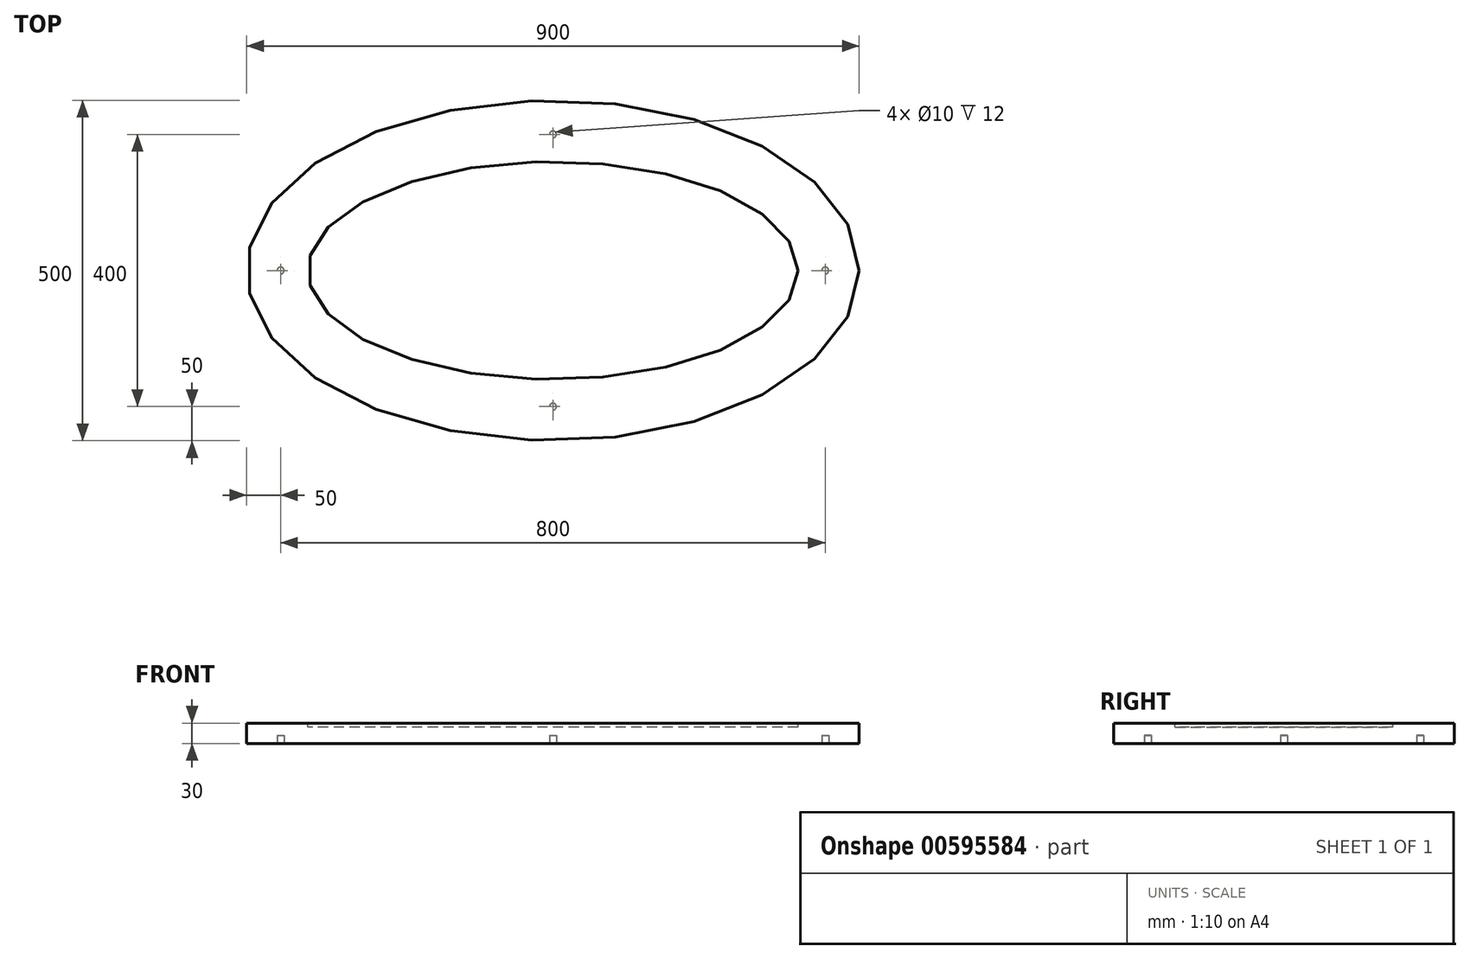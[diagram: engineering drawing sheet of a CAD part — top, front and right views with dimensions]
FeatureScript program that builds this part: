
annotation { "Feature Type Name" : "Feature", "Feature Type Description" : "" }
export const myFeature = defineFeature(function(context is Context, id is Id, definition is map)
    precondition{}
    {
        {
            var Q0;
            Q0=qCreatedBy(makeId("Top.planeOp"),FACE);
            var sketch = newSketch(context, id + "F0", { "sketchPlane" : qUnion([Q0])});
            skEllipse(sketch, "E0", {"center": v(0, 0) * mm, "majorRadius": 450 * mm, "minorRadius": 250 * mm, "majorAxis": v(1, 0)});
            skFitSpline(sketch, "E1.0", {"points": [v(349.97, -1.74) * mm, v(350.01, 0) * mm, v(349.97, 1.74) * mm, v(349.82, 4.08) * mm, v(349.42, 7.07) * mm, v(348.57, 10.9) * mm, v(347.27, 15.08) * mm, v(345.43, 19.64) * mm, v(342.94, 24.63) * mm, v(339.74, 30.04) * mm, v(335.72, 35.84) * mm, v(330.84, 41.98) * mm, v(325.03, 48.4) * mm, v(318.28, 55.05) * mm, v(310.55, 61.86) * mm, v(301.83, 68.75) * mm, v(293.75, 74.52) * mm, v(286.8, 79.12) * mm, v(281.33, 82.56) * mm, v(275.62, 85.98) * mm, v(269.67, 89.37) * mm, v(263.5, 92.72) * mm, v(257.12, 96) * mm, v(250.55, 99.23) * mm, v(241.54, 103.43) * mm, v(229.8, 108.51) * mm, v(215.03, 114.28) * mm, v(199.6, 119.7) * mm, v(178.22, 126.42) * mm, v(150.1, 133.81) * mm, v(120.4, 139.72) * mm, v(95.91, 143.5) * mm, v(77.2, 145.85) * mm, v(58.22, 147.69) * mm, v(42.2, 148.8) * mm, v(29.3, 149.42) * mm, v(19.56, 149.75) * mm, v(11.43, 149.92) * mm, v(4.9, 149.99) * mm, v(0, 150) * mm, v(-4.9, 149.99) * mm, v(-11.43, 149.92) * mm, v(-19.56, 149.75) * mm, v(-29.3, 149.42) * mm, v(-42.2, 148.8) * mm, v(-58.22, 147.69) * mm, v(-77.2, 145.85) * mm, v(-95.91, 143.5) * mm, v(-120.4, 139.72) * mm, v(-150.1, 133.81) * mm, v(-178.22, 126.42) * mm, v(-199.6, 119.7) * mm, v(-215.03, 114.28) * mm, v(-229.8, 108.51) * mm, v(-241.54, 103.43) * mm, v(-250.55, 99.23) * mm, v(-257.12, 96) * mm, v(-263.5, 92.72) * mm, v(-269.67, 89.37) * mm, v(-275.62, 85.98) * mm, v(-281.33, 82.56) * mm, v(-286.8, 79.12) * mm, v(-293.75, 74.52) * mm, v(-301.83, 68.75) * mm, v(-310.55, 61.86) * mm, v(-318.28, 55.05) * mm, v(-325.03, 48.4) * mm, v(-330.84, 41.98) * mm, v(-335.72, 35.84) * mm, v(-339.74, 30.04) * mm, v(-342.94, 24.63) * mm, v(-345.43, 19.64) * mm, v(-347.27, 15.08) * mm, v(-348.57, 10.9) * mm, v(-349.42, 7.07) * mm, v(-349.82, 4.08) * mm, v(-349.97, 1.74) * mm, v(-350.01, 0) * mm, v(-349.97, -1.74) * mm, v(-349.82, -4.08) * mm, v(-349.42, -7.07) * mm, v(-348.57, -10.9) * mm, v(-347.27, -15.08) * mm, v(-345.43, -19.64) * mm, v(-342.94, -24.63) * mm, v(-339.74, -30.04) * mm, v(-335.72, -35.84) * mm, v(-330.84, -41.98) * mm, v(-325.03, -48.4) * mm, v(-318.28, -55.05) * mm, v(-310.55, -61.86) * mm, v(-301.83, -68.75) * mm, v(-293.75, -74.52) * mm, v(-286.8, -79.12) * mm, v(-281.33, -82.56) * mm, v(-275.62, -85.98) * mm, v(-269.67, -89.37) * mm, v(-263.5, -92.72) * mm, v(-257.12, -96) * mm, v(-250.55, -99.23) * mm, v(-241.54, -103.43) * mm, v(-229.8, -108.51) * mm, v(-215.03, -114.28) * mm, v(-199.6, -119.7) * mm, v(-178.22, -126.42) * mm, v(-150.1, -133.81) * mm, v(-120.4, -139.72) * mm, v(-95.91, -143.5) * mm, v(-77.2, -145.85) * mm, v(-58.22, -147.69) * mm, v(-42.2, -148.8) * mm, v(-29.3, -149.42) * mm, v(-19.56, -149.75) * mm, v(-11.43, -149.92) * mm, v(-4.9, -149.99) * mm, v(0, -150) * mm, v(4.9, -149.99) * mm, v(11.43, -149.92) * mm, v(19.56, -149.75) * mm, v(29.3, -149.42) * mm, v(42.2, -148.8) * mm, v(58.22, -147.69) * mm, v(77.2, -145.85) * mm, v(95.91, -143.5) * mm, v(120.4, -139.72) * mm, v(150.1, -133.81) * mm, v(178.22, -126.42) * mm, v(199.6, -119.7) * mm, v(215.03, -114.28) * mm, v(229.8, -108.51) * mm, v(241.54, -103.43) * mm, v(250.55, -99.23) * mm, v(257.12, -96) * mm, v(263.5, -92.72) * mm, v(269.67, -89.37) * mm, v(275.62, -85.98) * mm, v(281.33, -82.56) * mm, v(286.8, -79.12) * mm, v(293.75, -74.52) * mm, v(301.83, -68.75) * mm, v(310.55, -61.86) * mm, v(318.28, -55.05) * mm, v(325.03, -48.4) * mm, v(330.84, -41.98) * mm, v(335.72, -35.84) * mm, v(339.74, -30.04) * mm, v(342.94, -24.63) * mm, v(345.43, -19.64) * mm, v(347.27, -15.08) * mm, v(348.57, -10.9) * mm, v(349.42, -7.07) * mm, v(349.82, -4.08) * mm, v(349.97, -1.74) * mm, v(350.01, 0) * mm, v(349.97, 1.74) * mm, v(349.97, -1.74) * mm]});
            skSolve(sketch);
        }
        {
            var Q0;
            Q0=makeQuery(id+"F0.imprint","IMPRINT",FACE,{"disambiguationData":[TD([[makeQuery(id+"F0.imprint","IMPRINT",EDGE,{"derivedFrom":sQuery(id+"F0.wireOp",EDGE,"E0")}),1.0]])]});
            extrude(context, id + "F1", {"entities" : qUnion([Q0]), "depth" : 30 * mm, "offsetDistance" : 25 * mm});
        }
        {
            var Q0;
            Q0=qCreatedBy(makeId("Top.planeOp"),FACE);
            cPlane(context, id + "F2", {"entities" : qUnion([Q0]), "cplaneType" : CPlaneType.OFFSET, "offset" : 30 * mm, "width" : 150 * mm, "height" : 150 * mm});
        }
        {
            var Q0;
            Q0=qCreatedBy(id+"F2.planeOp",FACE);
            var sketch = newSketch(context, id + "F3", { "sketchPlane" : qUnion([Q0])});
            skEllipse(sketch, "E2", {"center": v(0, 0) * mm, "majorRadius": 360 * mm, "minorRadius": 160 * mm, "majorAxis": v(1, 0)});
            skSolve(sketch);
        }
        {
            var Q0;
            Q0 = qSketchRegion(id + "F3", true);
            extrude(context, id + "F4", {"entities" : qUnion([Q0]), "operationType" : NewBodyOperationType.REMOVE, "oppositeDirection" : true, "depth" : 6 * mm, "offsetDistance" : 25 * mm});
        }
        {
            var Q0;
            Q0=makeQuery(id+"F1.opExtrude","CAP_FACE",FACE,{"disambiguationData":[OSD([sQuery(id+"F0.wireOp",EDGE,"E0"),sQuery(id+"F0.wireOp",EDGE,"E1.0")])],"isStart":true});
            var sketch = newSketch(context, id + "F5", { "sketchPlane" : qUnion([Q0])});
            skLineSegment(sketch, "E3", {"start": v(0, 0) * mm, "end": v(0, 220.57) * mm, "construction": true});
            skLineSegment(sketch, "E4.0", {"start": v(-300, 0) * mm, "end": v(-300, 220.57) * mm, "construction": true});
            skFitSpline(sketch, "E5.0", {"points": [v(399.96, 3.31) * mm, v(400.03, 0) * mm, v(399.96, -3.31) * mm, v(399.8, -5.96) * mm, v(399.65, -7.95) * mm, v(399.45, -9.93) * mm, v(399.2, -11.93) * mm, v(398.92, -13.92) * mm, v(398.59, -15.91) * mm, v(398.2, -17.9) * mm, v(397.78, -19.91) * mm, v(397.3, -21.93) * mm, v(396.79, -23.94) * mm, v(396.22, -25.96) * mm, v(395.6, -27.99) * mm, v(394.95, -30.03) * mm, v(394.23, -32.07) * mm, v(393.47, -34.12) * mm, v(392.39, -36.87) * mm, v(390.32, -41.7) * mm, v(385.44, -51.48) * mm, v(376.28, -65.74) * mm, v(364.02, -80.2) * mm, v(352.3, -91.73) * mm, v(342.55, -100.3) * mm, v(331.84, -108.77) * mm, v(322.13, -115.7) * mm, v(313.89, -121.15) * mm, v(307.48, -125.19) * mm, v(300.83, -129.16) * mm, v(293.95, -133.08) * mm, v(286.86, -136.92) * mm, v(279.59, -140.67) * mm, v(272.14, -144.33) * mm, v(261.96, -149.08) * mm, v(248.82, -154.77) * mm, v(232.4, -161.18) * mm, v(215.37, -167.16) * mm, v(191.9, -174.53) * mm, v(161.29, -182.57) * mm, v(129.2, -188.96) * mm, v(102.82, -193.03) * mm, v(82.73, -195.55) * mm, v(62.36, -197.52) * mm, v(45.19, -198.7) * mm, v(31.36, -199.38) * mm, v(20.94, -199.74) * mm, v(12.23, -199.92) * mm, v(5.25, -199.99) * mm, v(0, -200) * mm, v(-5.25, -199.99) * mm, v(-12.23, -199.92) * mm, v(-20.94, -199.74) * mm, v(-31.36, -199.38) * mm, v(-45.19, -198.7) * mm, v(-62.36, -197.52) * mm, v(-82.73, -195.55) * mm, v(-102.82, -193.03) * mm, v(-129.2, -188.96) * mm, v(-161.29, -182.57) * mm, v(-191.9, -174.53) * mm, v(-215.37, -167.16) * mm, v(-232.4, -161.18) * mm, v(-248.82, -154.77) * mm, v(-261.96, -149.08) * mm, v(-272.14, -144.33) * mm, v(-279.59, -140.67) * mm, v(-286.86, -136.92) * mm, v(-293.95, -133.08) * mm, v(-300.83, -129.16) * mm, v(-307.48, -125.19) * mm, v(-313.89, -121.15) * mm, v(-322.13, -115.7) * mm, v(-331.84, -108.77) * mm, v(-342.55, -100.3) * mm, v(-352.3, -91.73) * mm, v(-364.02, -80.2) * mm, v(-376.28, -65.74) * mm, v(-385.44, -51.48) * mm, v(-390.32, -41.7) * mm, v(-392.39, -36.87) * mm, v(-393.47, -34.12) * mm, v(-394.23, -32.07) * mm, v(-394.95, -30.03) * mm, v(-395.6, -27.99) * mm, v(-396.22, -25.96) * mm, v(-396.79, -23.94) * mm, v(-397.3, -21.93) * mm, v(-397.78, -19.91) * mm, v(-398.2, -17.9) * mm, v(-398.59, -15.91) * mm, v(-398.92, -13.92) * mm, v(-399.2, -11.93) * mm, v(-399.45, -9.93) * mm, v(-399.65, -7.95) * mm, v(-399.8, -5.96) * mm, v(-399.96, -3.31) * mm, v(-400.03, 0) * mm, v(-399.96, 3.31) * mm, v(-399.8, 5.96) * mm, v(-399.65, 7.95) * mm, v(-399.45, 9.93) * mm, v(-399.2, 11.93) * mm, v(-398.92, 13.92) * mm, v(-398.59, 15.91) * mm, v(-398.2, 17.9) * mm, v(-397.78, 19.91) * mm, v(-397.3, 21.93) * mm, v(-396.79, 23.94) * mm, v(-396.22, 25.96) * mm, v(-395.6, 27.99) * mm, v(-394.95, 30.03) * mm, v(-394.23, 32.07) * mm, v(-393.47, 34.12) * mm, v(-392.39, 36.87) * mm, v(-390.32, 41.7) * mm, v(-385.44, 51.48) * mm, v(-376.28, 65.74) * mm, v(-364.02, 80.2) * mm, v(-352.3, 91.73) * mm, v(-342.55, 100.3) * mm, v(-331.84, 108.77) * mm, v(-322.13, 115.7) * mm, v(-313.89, 121.15) * mm, v(-307.48, 125.19) * mm, v(-300.83, 129.16) * mm, v(-293.95, 133.08) * mm, v(-286.86, 136.92) * mm, v(-279.59, 140.67) * mm, v(-272.14, 144.33) * mm, v(-261.96, 149.08) * mm, v(-248.82, 154.77) * mm, v(-232.4, 161.18) * mm, v(-215.37, 167.16) * mm, v(-191.9, 174.53) * mm, v(-161.29, 182.57) * mm, v(-129.2, 188.96) * mm, v(-102.82, 193.03) * mm, v(-82.73, 195.55) * mm, v(-62.36, 197.52) * mm, v(-45.19, 198.7) * mm, v(-31.36, 199.38) * mm, v(-20.94, 199.74) * mm, v(-12.23, 199.92) * mm, v(-5.25, 199.99) * mm, v(0, 200) * mm, v(5.25, 199.99) * mm, v(12.23, 199.92) * mm, v(20.94, 199.74) * mm, v(31.36, 199.38) * mm, v(45.19, 198.7) * mm, v(62.36, 197.52) * mm, v(82.73, 195.55) * mm, v(102.82, 193.03) * mm, v(129.2, 188.96) * mm, v(161.29, 182.57) * mm, v(191.9, 174.53) * mm, v(215.37, 167.16) * mm, v(232.4, 161.18) * mm, v(248.82, 154.77) * mm, v(261.96, 149.08) * mm, v(272.14, 144.33) * mm, v(279.59, 140.67) * mm, v(286.86, 136.92) * mm, v(293.95, 133.08) * mm, v(300.83, 129.16) * mm, v(307.48, 125.19) * mm, v(313.89, 121.15) * mm, v(322.13, 115.7) * mm, v(331.84, 108.77) * mm, v(342.55, 100.3) * mm, v(352.3, 91.73) * mm, v(364.02, 80.2) * mm, v(376.28, 65.74) * mm, v(385.44, 51.48) * mm, v(390.32, 41.7) * mm, v(392.39, 36.87) * mm, v(393.47, 34.12) * mm, v(394.23, 32.07) * mm, v(394.95, 30.03) * mm, v(395.6, 27.99) * mm, v(396.22, 25.96) * mm, v(396.79, 23.94) * mm, v(397.3, 21.93) * mm, v(397.78, 19.91) * mm, v(398.2, 17.9) * mm, v(398.59, 15.91) * mm, v(398.92, 13.92) * mm, v(399.2, 11.93) * mm, v(399.45, 9.93) * mm, v(399.65, 7.95) * mm, v(399.8, 5.96) * mm, v(399.96, 3.31) * mm, v(400.03, 0) * mm, v(399.96, -3.31) * mm, v(399.96, 3.31) * mm], "construction": true});
            skFitSpline(sketch, "E6.0", {"points": [v(444.91, -5.99) * mm, v(445.04, 0) * mm, v(444.91, 5.99) * mm, v(444.38, 13.94) * mm, v(443.05, 23.84) * mm, v(440.41, 35.64) * mm, v(435.51, 51.22) * mm, v(426.83, 70.41) * mm, v(412.4, 92.81) * mm, v(397.08, 110.82) * mm, v(382.92, 124.74) * mm, v(371.35, 134.9) * mm, v(358.85, 144.79) * mm, v(347.67, 152.76) * mm, v(338.28, 158.97) * mm, v(331, 163.55) * mm, v(324.76, 167.28) * mm, v(319.66, 170.23) * mm, v(315.78, 172.41) * mm, v(311.85, 174.57) * mm, v(306.54, 177.4) * mm, v(299.8, 180.88) * mm, v(291.56, 184.93) * mm, v(280.34, 190.16) * mm, v(265.92, 196.4) * mm, v(248.02, 203.4) * mm, v(229.55, 209.88) * mm, v(204.23, 217.83) * mm, v(171.36, 226.46) * mm, v(137.12, 233.27) * mm, v(109.05, 237.6) * mm, v(87.7, 240.28) * mm, v(66.07, 242.38) * mm, v(47.87, 243.63) * mm, v(33.22, 244.34) * mm, v(22.18, 244.72) * mm, v(12.96, 244.91) * mm, v(5.56, 244.99) * mm, v(0, 245) * mm, v(-5.56, 244.99) * mm, v(-12.96, 244.91) * mm, v(-22.18, 244.72) * mm, v(-33.22, 244.34) * mm, v(-47.87, 243.63) * mm, v(-66.07, 242.38) * mm, v(-87.7, 240.28) * mm, v(-109.05, 237.6) * mm, v(-137.12, 233.27) * mm, v(-171.36, 226.46) * mm, v(-204.23, 217.83) * mm, v(-229.55, 209.88) * mm, v(-248.02, 203.4) * mm, v(-265.92, 196.4) * mm, v(-280.34, 190.16) * mm, v(-291.56, 184.93) * mm, v(-299.8, 180.88) * mm, v(-306.54, 177.4) * mm, v(-311.85, 174.57) * mm, v(-315.78, 172.41) * mm, v(-319.66, 170.23) * mm, v(-324.76, 167.28) * mm, v(-331, 163.55) * mm, v(-338.28, 158.97) * mm, v(-347.67, 152.76) * mm, v(-358.85, 144.79) * mm, v(-371.35, 134.9) * mm, v(-382.92, 124.74) * mm, v(-397.08, 110.82) * mm, v(-412.4, 92.81) * mm, v(-426.83, 70.41) * mm, v(-435.51, 51.22) * mm, v(-440.41, 35.64) * mm, v(-443.05, 23.84) * mm, v(-444.38, 13.94) * mm, v(-444.91, 5.99) * mm, v(-445.04, 0) * mm, v(-444.91, -5.99) * mm, v(-444.38, -13.94) * mm, v(-443.05, -23.84) * mm, v(-440.41, -35.64) * mm, v(-435.51, -51.22) * mm, v(-426.83, -70.41) * mm, v(-412.4, -92.81) * mm, v(-397.08, -110.82) * mm, v(-382.92, -124.74) * mm, v(-371.35, -134.9) * mm, v(-358.85, -144.79) * mm, v(-347.67, -152.76) * mm, v(-338.28, -158.97) * mm, v(-331, -163.55) * mm, v(-324.76, -167.28) * mm, v(-319.66, -170.23) * mm, v(-315.78, -172.41) * mm, v(-311.85, -174.57) * mm, v(-306.54, -177.4) * mm, v(-299.8, -180.88) * mm, v(-291.56, -184.93) * mm, v(-280.34, -190.16) * mm, v(-265.92, -196.4) * mm, v(-248.02, -203.4) * mm, v(-229.55, -209.88) * mm, v(-204.23, -217.83) * mm, v(-171.36, -226.46) * mm, v(-137.12, -233.27) * mm, v(-109.05, -237.6) * mm, v(-87.7, -240.28) * mm, v(-66.07, -242.38) * mm, v(-47.87, -243.63) * mm, v(-33.22, -244.34) * mm, v(-22.18, -244.72) * mm, v(-12.96, -244.91) * mm, v(-5.56, -244.99) * mm, v(0, -245) * mm, v(5.56, -244.99) * mm, v(12.96, -244.91) * mm, v(22.18, -244.72) * mm, v(33.22, -244.34) * mm, v(47.87, -243.63) * mm, v(66.07, -242.38) * mm, v(87.7, -240.28) * mm, v(109.05, -237.6) * mm, v(137.12, -233.27) * mm, v(171.36, -226.46) * mm, v(204.23, -217.83) * mm, v(229.55, -209.88) * mm, v(248.02, -203.4) * mm, v(265.92, -196.4) * mm, v(280.34, -190.16) * mm, v(291.56, -184.93) * mm, v(299.8, -180.88) * mm, v(306.54, -177.4) * mm, v(311.85, -174.57) * mm, v(315.78, -172.41) * mm, v(319.66, -170.23) * mm, v(324.76, -167.28) * mm, v(331, -163.55) * mm, v(338.28, -158.97) * mm, v(347.67, -152.76) * mm, v(358.85, -144.79) * mm, v(371.35, -134.9) * mm, v(382.92, -124.74) * mm, v(397.08, -110.82) * mm, v(412.4, -92.81) * mm, v(426.83, -70.41) * mm, v(435.51, -51.22) * mm, v(440.41, -35.64) * mm, v(443.05, -23.84) * mm, v(444.38, -13.94) * mm, v(444.91, -5.99) * mm, v(445.04, 0) * mm, v(444.91, 5.99) * mm, v(444.91, -5.99) * mm], "construction": true});
            skLineSegment(sketch, "E7", {"start": v(0, 0) * mm, "end": v(0, -277.53) * mm, "construction": true});
            skLineSegment(sketch, "E8", {"start": v(0, 0) * mm, "end": v(560.25, 0) * mm, "construction": true});
            skCircle(sketch, "E9", {"center": v(0, -200) * mm, "radius": 5 * mm});
            skCircle(sketch, "E10.MirrorC", {"center": v(0, 200) * mm, "radius": 5 * mm});
            skCircle(sketch, "E11", {"center": v(400, 0) * mm, "radius": 5 * mm});
            skCircle(sketch, "E12.MirrorC", {"center": v(-400, 0) * mm, "radius": 5 * mm});
            skSolve(sketch);
        }
        {
            var Q0;
            Q0 = qSketchRegion(id + "F5", true);
            extrude(context, id + "F6", {"entities" : qUnion([Q0]), "operationType" : NewBodyOperationType.REMOVE, "oppositeDirection" : true, "depth" : 12 * mm, "offsetDistance" : 25 * mm});
        }
    });
